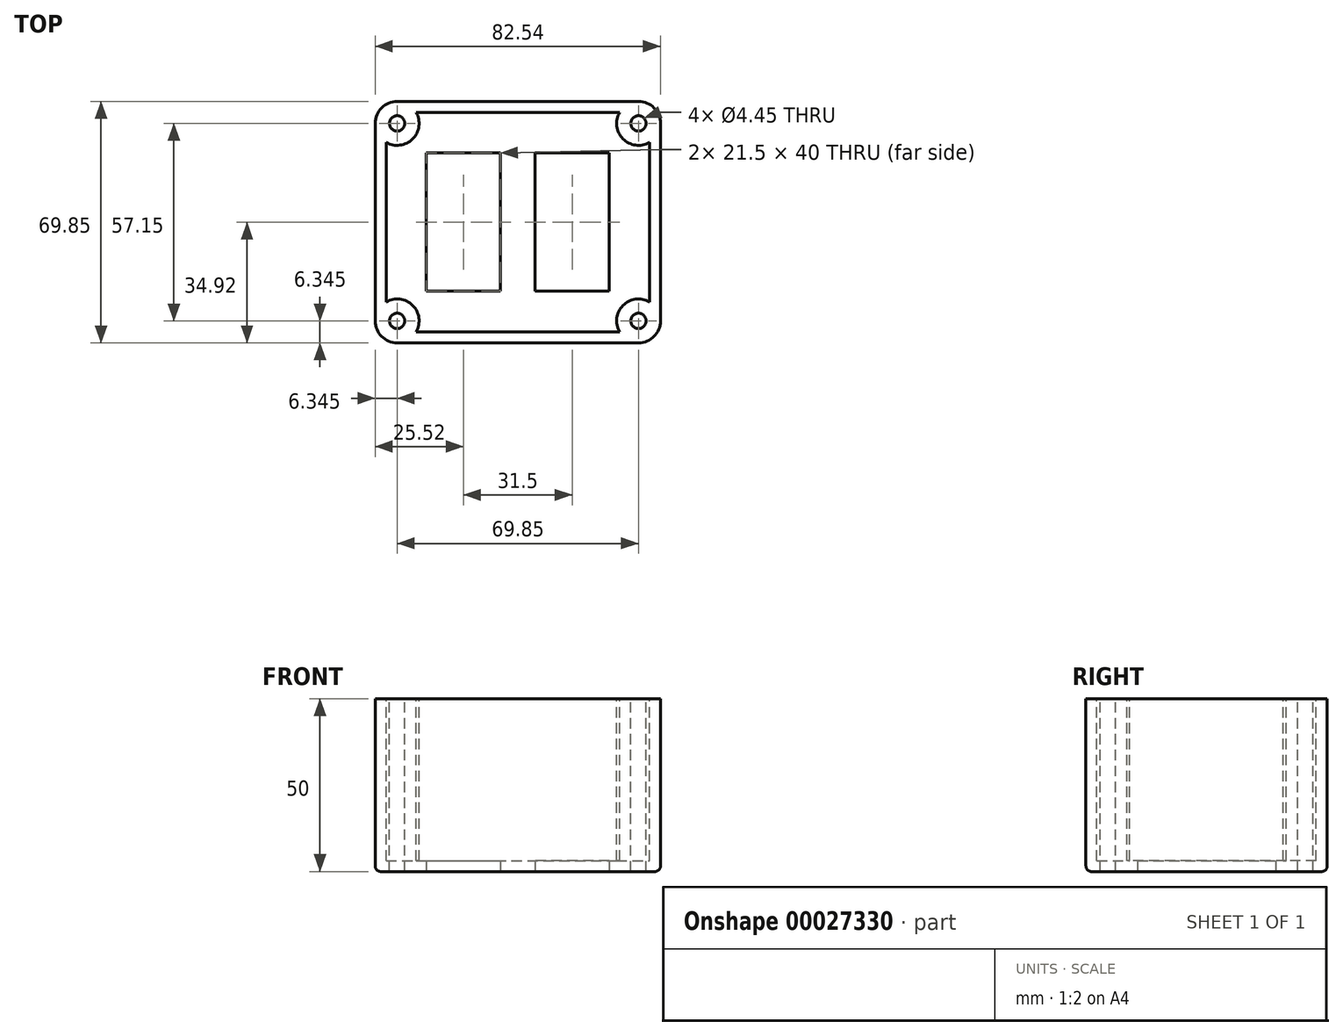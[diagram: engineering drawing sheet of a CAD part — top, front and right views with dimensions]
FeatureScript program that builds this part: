
annotation { "Feature Type Name" : "Feature", "Feature Type Description" : "" }
export const myFeature = defineFeature(function(context is Context, id is Id, definition is map)
    precondition{}
    {
        {
            var Q0;
            Q0=qCreatedBy(makeId("Top.planeOp"),FACE);
            var sketch = newSketch(context, id + "F0", { "sketchPlane" : qUnion([Q0])});
            skLineSegment(sketch, "E0.bottom", {"start": v(-5, 20) * mm, "end": v(-26.5, 20) * mm});
            skLineSegment(sketch, "E0.top", {"start": v(-5, -20) * mm, "end": v(-26.5, -20) * mm});
            skLineSegment(sketch, "E0.left", {"start": v(-5, 20) * mm, "end": v(-5, -20) * mm});
            skLineSegment(sketch, "E0.right", {"start": v(-26.5, 20) * mm, "end": v(-26.5, -20) * mm});
            skLineSegment(sketch, "E1.bottom", {"start": v(5, 20) * mm, "end": v(26.5, 20) * mm});
            skLineSegment(sketch, "E1.top", {"start": v(5, -20) * mm, "end": v(26.5, -20) * mm});
            skLineSegment(sketch, "E1.left", {"start": v(5, 20) * mm, "end": v(5, -20) * mm});
            skLineSegment(sketch, "E1.right", {"start": v(26.5, 20) * mm, "end": v(26.5, -20) * mm});
            skLineSegment(sketch, "E2", {"start": v(-5, 0) * mm, "end": v(5, 0) * mm, "construction": true});
            skLineSegment(sketch, "E3.bottom", {"start": v(-41.28, 34.93) * mm, "end": v(41.28, 34.93) * mm});
            skLineSegment(sketch, "E3.top", {"start": v(-41.28, -34.92) * mm, "end": v(41.27, -34.92) * mm});
            skLineSegment(sketch, "E3.left", {"start": v(-41.28, 34.93) * mm, "end": v(-41.28, -34.93) * mm});
            skLineSegment(sketch, "E3.right", {"start": v(41.28, 34.93) * mm, "end": v(41.27, -34.92) * mm});
            skLineSegment(sketch, "E4", {"start": v(-41.28, -34.93) * mm, "end": v(41.27, 34.93) * mm, "construction": true});
            skSolve(sketch);
        }
        {
            var Q0;
            Q0 = qSketchRegion(id + "F0", true);
            var Q1;
            Q1=makeQuery(id+"F0.imprint","IMPRINT",FACE,{"disambiguationData":[TD([[makeQuery(id+"F0.imprint","IMPRINT",EDGE,{"derivedFrom":sQuery(id+"F0.wireOp",EDGE,"E0.bottom")}),1.0]])]});
            var Q2;
            Q2=makeQuery(id+"F0.imprint","IMPRINT",FACE,{"disambiguationData":[TD([[makeQuery(id+"F0.imprint","IMPRINT",EDGE,{"derivedFrom":sQuery(id+"F0.wireOp",EDGE,"E1.bottom")}),-1.0]])]});
            extrude(context, id + "F1", {"entities" : qUnion([Q0, Q1, Q2]), "depth" : 50 * mm});
        }
        {
            var Q0;
            Q0=makeQuery(id+"F1.opExtrude","CAP_FACE",FACE,{"disambiguationData":[OSD([sQuery(id+"F0.wireOp",EDGE,"E3.bottom"),sQuery(id+"F0.wireOp",EDGE,"E3.top"),sQuery(id+"F0.wireOp",EDGE,"E3.left"),sQuery(id+"F0.wireOp",EDGE,"E3.right")])],"isStart":false});
            shell(context, id + "F2", {"entities" : qUnion([Q0]), "thickness" : 3.17 * mm});
        }
        {
            var Q0;
            Q0=makeQuery(id+"F0.imprint","IMPRINT",FACE,{"disambiguationData":[TD([[makeQuery(id+"F0.imprint","IMPRINT",EDGE,{"derivedFrom":sQuery(id+"F0.wireOp",EDGE,"E0.bottom")}),1.0]])]});
            var Q1;
            Q1=makeQuery(id+"F0.imprint","IMPRINT",FACE,{"disambiguationData":[TD([[makeQuery(id+"F0.imprint","IMPRINT",EDGE,{"derivedFrom":sQuery(id+"F0.wireOp",EDGE,"E1.bottom")}),-1.0]])]});
            extrude(context, id + "F3", {"entities" : qUnion([Q0, Q1]), "operationType" : NewBodyOperationType.REMOVE, "endBound" : BoundingType.THROUGH_ALL, "depth" : 25.4 * mm});
        }
        {
            var Q0;
            Q0=makeQuery(id+"F1.opExtrude","CAP_FACE",FACE,{"disambiguationData":[OSD([sQuery(id+"F0.wireOp",EDGE,"E3.bottom"),sQuery(id+"F0.wireOp",EDGE,"E3.top"),sQuery(id+"F0.wireOp",EDGE,"E3.left"),sQuery(id+"F0.wireOp",EDGE,"E3.right")])],"isStart":false});
            var sketch = newSketch(context, id + "F4", { "sketchPlane" : qUnion([Q0])});
            skCircle(sketch, "E5", {"center": v(-34.93, 28.58) * mm, "radius": 6.35 * mm});
            skCircle(sketch, "E6", {"center": v(-34.93, -28.57) * mm, "radius": 6.35 * mm});
            skCircle(sketch, "E7", {"center": v(34.92, -28.57) * mm, "radius": 6.35 * mm});
            skCircle(sketch, "E8", {"center": v(34.93, 28.58) * mm, "radius": 6.35 * mm});
            skSolve(sketch);
        }
        {
            var Q0;
            Q0 = qSketchRegion(id + "F4", true);
            var Q1;
            Q1=makeQuery(id+"F2.opShell","OFFSET_FACE",FACE,{"disambiguationData":[OSD([sQuery(id+"F0.wireOp",EDGE,"E3.bottom"),sQuery(id+"F0.wireOp",EDGE,"E3.top"),sQuery(id+"F0.wireOp",EDGE,"E3.left"),sQuery(id+"F0.wireOp",EDGE,"E3.right")])]});
            extrude(context, id + "F5", {"entities" : qUnion([Q0]), "operationType" : NewBodyOperationType.ADD, "endBound" : BoundingType.UP_TO_SURFACE, "oppositeDirection" : true, "endBoundEntityFace" : qUnion([Q1]), "depth" : 25.4 * mm});
        }
        {
            var Q0;
            Q0=makeQuery(id+"F1.opExtrude","SWEPT_EDGE",EDGE,{"disambiguationData":[OSD([sQuery(id+"F0.wireOp",EDGE,"E3.top"),sQuery(id+"F0.wireOp",EDGE,"E3.left")])]});
            var Q1;
            Q1=makeQuery(id+"F1.opExtrude","SWEPT_EDGE",EDGE,{"disambiguationData":[OSD([sQuery(id+"F0.wireOp",EDGE,"E3.top"),sQuery(id+"F0.wireOp",EDGE,"E3.right")])]});
            var Q2;
            Q2=makeQuery(id+"F1.opExtrude","SWEPT_EDGE",EDGE,{"disambiguationData":[OSD([sQuery(id+"F0.wireOp",EDGE,"E3.bottom"),sQuery(id+"F0.wireOp",EDGE,"E3.right")])]});
            var Q3;
            Q3=makeQuery(id+"F1.opExtrude","SWEPT_EDGE",EDGE,{"disambiguationData":[OSD([sQuery(id+"F0.wireOp",EDGE,"E3.bottom"),sQuery(id+"F0.wireOp",EDGE,"E3.left")])]});
            fillet(context, id + "F6", {"entities" : qUnion([Q0, Q1, Q2, Q3]), "radius" : 6.35 * mm, "tangentPropagation" : true, "allowEdgeOverflow" : false});
        }
        {
            var Q0;
            Q0=makeQuery(id+"F1.opExtrude","CAP_EDGE",EDGE,{"disambiguationData":[OSD([sQuery(id+"F0.wireOp",EDGE,"E3.bottom")])],"isStart":true});
            fillet(context, id + "F7", {"entities" : qUnion([Q0]), "radius" : 1.59 * mm, "tangentPropagation" : true, "allowEdgeOverflow" : false});
        }
        {
            var Q0;
            Q0=makeQuery(id+"F5.boolean.opBoolean","MERGE",FACE,{"derivedFrom":[makeQuery(id+"F1.opExtrude","CAP_FACE",FACE,{"disambiguationData":[OSD([sQuery(id+"F0.wireOp",EDGE,"E3.bottom"),sQuery(id+"F0.wireOp",EDGE,"E3.top"),sQuery(id+"F0.wireOp",EDGE,"E3.left"),sQuery(id+"F0.wireOp",EDGE,"E3.right")])],"isStart":false}),makeQuery(id+"F5.opExtrude","CAP_FACE",FACE,{"disambiguationData":[OSD([sQuery(id+"F4.wireOp",EDGE,"E5")])],"isStart":true}),makeQuery(id+"F5.opExtrude","CAP_FACE",FACE,{"disambiguationData":[OSD([sQuery(id+"F4.wireOp",EDGE,"E6")])],"isStart":true}),makeQuery(id+"F5.opExtrude","CAP_FACE",FACE,{"disambiguationData":[OSD([sQuery(id+"F4.wireOp",EDGE,"E7")])],"isStart":true}),makeQuery(id+"F5.opExtrude","CAP_FACE",FACE,{"disambiguationData":[OSD([sQuery(id+"F4.wireOp",EDGE,"E8")])],"isStart":true})]});
            var sketch = newSketch(context, id + "F8", { "sketchPlane" : qUnion([Q0])});
            skCircle(sketch, "E9", {"center": v(-34.93, 28.58) * mm, "radius": 2.22 * mm});
            skCircle(sketch, "E10", {"center": v(34.93, 28.58) * mm, "radius": 2.22 * mm});
            skCircle(sketch, "E11", {"center": v(34.92, -28.57) * mm, "radius": 2.22 * mm});
            skCircle(sketch, "E12", {"center": v(-34.93, -28.57) * mm, "radius": 2.22 * mm});
            skSolve(sketch);
        }
        {
            var Q0;
            Q0=makeQuery(id+"F8.imprint","IMPRINT",FACE,{"disambiguationData":[TD([[makeQuery(id+"F8.imprint","IMPRINT",EDGE,{"derivedFrom":sQuery(id+"F8.wireOp",EDGE,"E9")}),1.0]])]});
            var Q1;
            Q1=makeQuery(id+"F8.imprint","IMPRINT",FACE,{"disambiguationData":[TD([[makeQuery(id+"F8.imprint","IMPRINT",EDGE,{"derivedFrom":sQuery(id+"F8.wireOp",EDGE,"E10")}),1.0]])]});
            var Q2;
            Q2=makeQuery(id+"F8.imprint","IMPRINT",FACE,{"disambiguationData":[TD([[makeQuery(id+"F8.imprint","IMPRINT",EDGE,{"derivedFrom":sQuery(id+"F8.wireOp",EDGE,"E11")}),1.0]])]});
            var Q3;
            Q3=makeQuery(id+"F8.imprint","IMPRINT",FACE,{"disambiguationData":[TD([[makeQuery(id+"F8.imprint","IMPRINT",EDGE,{"derivedFrom":sQuery(id+"F8.wireOp",EDGE,"E12")}),1.0]])]});
            extrude(context, id + "F9", {"entities" : qUnion([Q0, Q1, Q2, Q3]), "operationType" : NewBodyOperationType.REMOVE, "endBound" : BoundingType.THROUGH_ALL, "oppositeDirection" : true, "depth" : 25.4 * mm});
        }
    });
